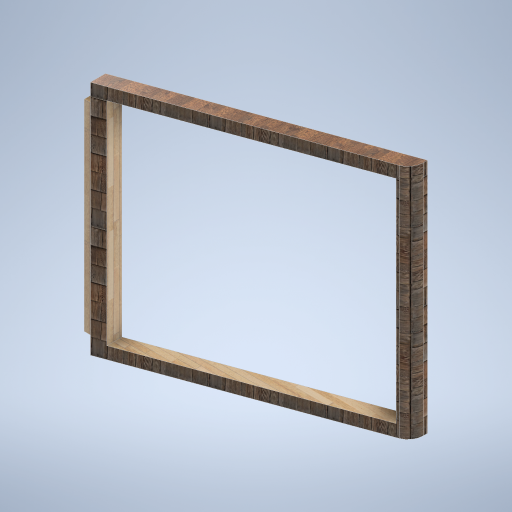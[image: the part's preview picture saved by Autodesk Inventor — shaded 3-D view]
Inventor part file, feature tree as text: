
AUTODESK INVENTOR PART (.ipt)
format: ipt  version: 2024.2 (Build 282272000, 272)  size: 394,752 bytes
history: native  units: mm
features: sketch x5, extrude x4, projected_geometry x2, plane x1, fillet x1
ambient origin geometry x8: Origin, YZ Plane, XZ Plane, XY Plane, X Axis, Y Axis, Z Axis, Center Point
bodies: Solid1 (feature_tree)
feature tree (13):
  extrude  "Extrusion1"  Depth=60.0mm TaperAngle=0.0deg
  sketch  "Sketch2"  dims[d6=2500.0mm d7=12.217305mm]
  plane  "Work Plane1"
  extrude  "Extrusion2"  Depth=12.217305mm
  extrude  "Extrusion3"  Depth=2351.0mm TaperAngle=0.0deg
  fillet  "Fillet1"  Radius=120.0mm
  extrude  "Extrusion4"  Depth=120.0mm
  sketch  "Sketch1"  dims[d3=150.0mm d4=60.0mm d5=0.0mm]
  projected_geometry  "Projected Loop1"
  sketch  "Sketch3"  dims[d8=12.217305mm d9=2351.0mm d10=0.0mm d11=120.0mm]
  sketch  "Sketch4"  dims[d12=120.0mm d13=120.0mm]
  projected_geometry  "Projected Loop2"
  sketch  "Sketch5"  dims[d14=120.0mm d15=0.0mm d16=0.0mm d17=150.0mm d18=0.0mm d19=0.0mm d20=0.0mm]
